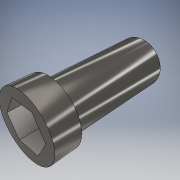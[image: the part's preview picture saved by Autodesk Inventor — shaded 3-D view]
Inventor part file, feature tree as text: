
AUTODESK INVENTOR PART (.ipt)
format: ipt  version: 2018 (Build 220112000, 112)  size: 140,800 bytes
history: native  units: mm
features: extrude x4, sketch x4, other x1
ambient origin geometry x8: Origin, YZ Plane, XZ Plane, XY Plane, X Axis, Y Axis, Z Axis, Center Point
bodies: Body1 (feature_tree)
feature tree (9):
  extrude  "Vysunutí2"  Depth=16.0mm TaperAngle=0.0deg
  extrude  "Vysunutí3"  Depth=3.0mm TaperAngle=0.0deg
  extrude  "Vysunutí4"  Depth=13.0mm TaperAngle=0.0deg
  extrude  "Vysunutí5"  Depth=10.0mm TaperAngle=0.0deg
  other  "Závit2"
  sketch  "Náčrt1"
  sketch  "Náčrt3"
  sketch  "Náčrt4"
  sketch  "Náčrt5"
